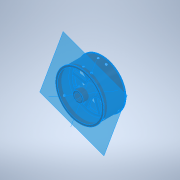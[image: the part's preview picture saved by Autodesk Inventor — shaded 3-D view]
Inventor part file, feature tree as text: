
AUTODESK INVENTOR PART (.ipt)
format: ipt  version: 2020 (Build 240168000, 168)  size: 327,168 bytes
history: native  units: in
note: dims shown in document units (in); Inventor stores cm internally (conversion verified against a paired STEP export)
features: sketch x2, plane x2, extrude x1, pattern_circular x1
ambient origin geometry x8: Origin, YZ Plane, XZ Plane, XY Plane, X Axis, Y Axis, Z Axis, Center Point
bodies: Solid1 (feature_tree)
feature tree (6):
  extrude  "Extrusion1"  Depth=1.0in TaperAngle=0.0deg
  sketch  "Sketch3"  dims[d15=0.47in d16=1.1811in d18=0.0in d20=1.1811in d22=0.0in d27=120.0deg d28=120.0deg d29=0.6184in d30=0.6184in d31=0.1in d32=0.4992in d33=3.5203in d34=3.7699in d35=3.5203in d36=3.6in]
  plane  "Work Plane2"
  plane  "Work Plane3"
  sketch  "Sketch2"  dims[d9=1.0in d10=0.0in d11=1.1811in d13=0.0in]
  pattern_circular  "CirPattern3"
